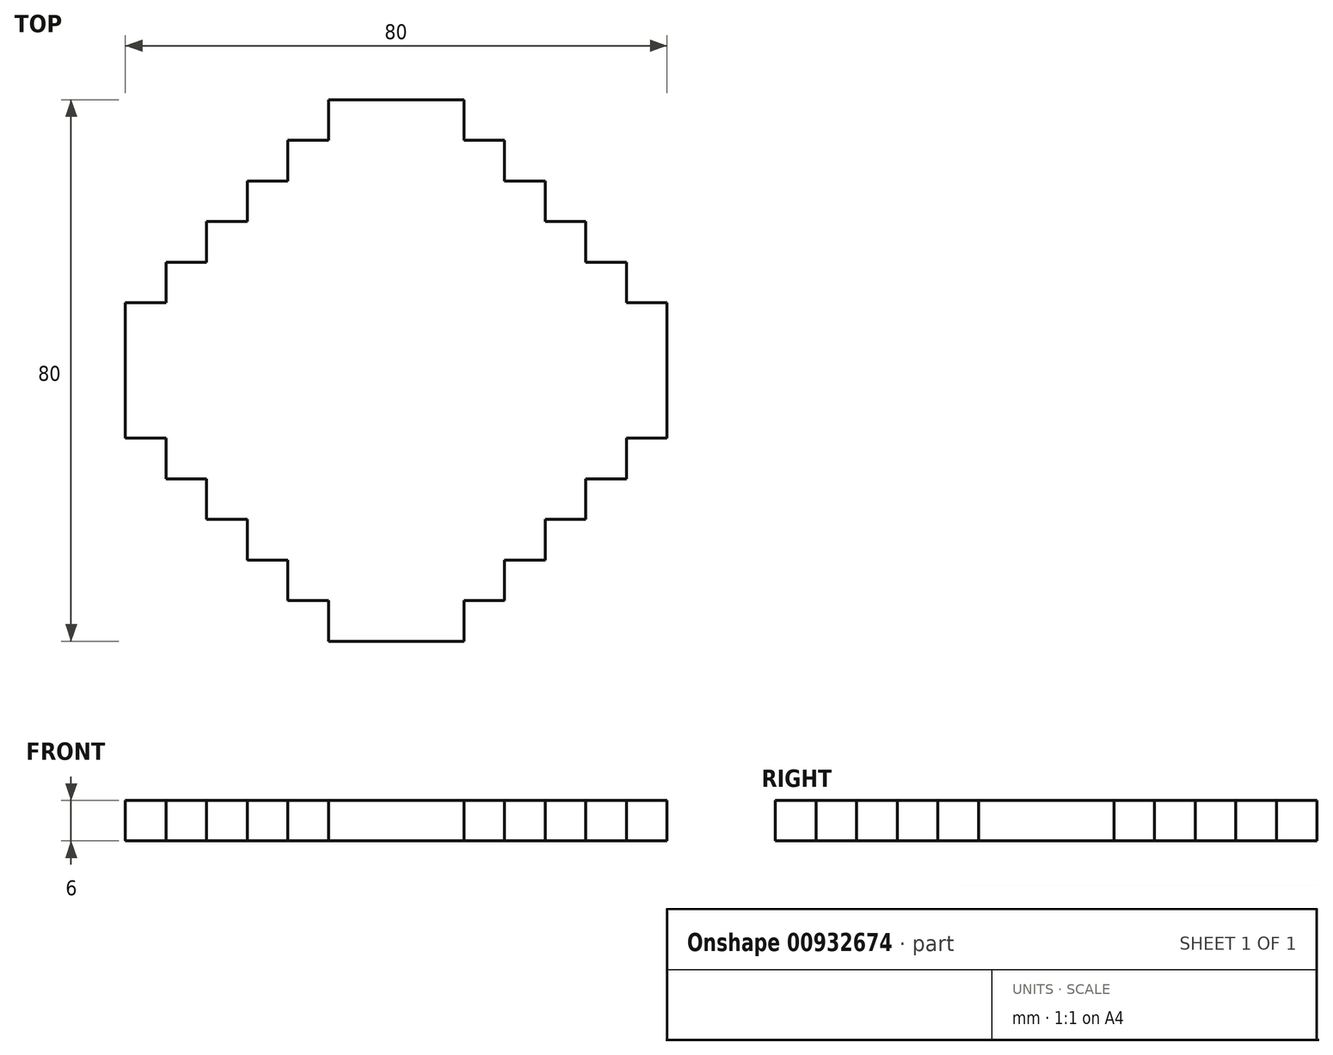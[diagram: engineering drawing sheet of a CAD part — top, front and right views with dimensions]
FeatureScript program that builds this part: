
annotation { "Feature Type Name" : "Feature", "Feature Type Description" : "" }
export const myFeature = defineFeature(function(context is Context, id is Id, definition is map)
    precondition{}
    {
        {
            var Q0;
            Q0=qCreatedBy(makeId("Top.planeOp"),FACE);
            var sketch = newSketch(context, id + "F0", { "sketchPlane" : qUnion([Q0])});
            skLineSegment(sketch, "E0.bottom", {"start": v(-10, 40) * mm, "end": v(10, 40) * mm});
            skLineSegment(sketch, "E0.top", {"start": v(-10, -40) * mm, "end": v(10, -40) * mm});
            skPoint(sketch, "E0.middle", {"position": v(0, 0) * mm});
            skLineSegment(sketch, "E1.top", {"start": v(10, 34) * mm, "end": v(16, 34) * mm});
            skLineSegment(sketch, "E1.left", {"start": v(10, 40) * mm, "end": v(10, 34) * mm});
            skLineSegment(sketch, "E2.top", {"start": v(16, 28) * mm, "end": v(22, 28) * mm});
            skLineSegment(sketch, "E2.left", {"start": v(16, 34) * mm, "end": v(16, 28) * mm});
            skLineSegment(sketch, "E3.top", {"start": v(22, 22) * mm, "end": v(28, 22) * mm});
            skLineSegment(sketch, "E3.left", {"start": v(22, 28) * mm, "end": v(22, 22) * mm});
            skLineSegment(sketch, "E4.top", {"start": v(28, 16) * mm, "end": v(34, 16) * mm});
            skLineSegment(sketch, "E4.left", {"start": v(28, 22) * mm, "end": v(28, 16) * mm});
            skLineSegment(sketch, "E5.top", {"start": v(34, 10) * mm, "end": v(40, 10) * mm});
            skLineSegment(sketch, "E5.left", {"start": v(34, 16) * mm, "end": v(34, 10) * mm});
            skLineSegment(sketch, "E6.MirrorCS", {"start": v(-16, 34) * mm, "end": v(-16, 28) * mm});
            skLineSegment(sketch, "E7.MirrorCS", {"start": v(-10, 40) * mm, "end": v(-10, 34) * mm});
            skLineSegment(sketch, "E8.MirrorCS", {"start": v(-22, 28) * mm, "end": v(-22, 22) * mm});
            skLineSegment(sketch, "E9.MirrorCS", {"start": v(-34, 16) * mm, "end": v(-34, 10) * mm});
            skLineSegment(sketch, "E10.MirrorCS", {"start": v(-28, 22) * mm, "end": v(-28, 16) * mm});
            skLineSegment(sketch, "E11.MirrorCS", {"start": v(-22, 22) * mm, "end": v(-28, 22) * mm});
            skLineSegment(sketch, "E12.MirrorCS", {"start": v(-28, 16) * mm, "end": v(-34, 16) * mm});
            skLineSegment(sketch, "E13.MirrorCS", {"start": v(-34, 10) * mm, "end": v(-40, 10) * mm});
            skLineSegment(sketch, "E14.MirrorCS", {"start": v(-16, 28) * mm, "end": v(-22, 28) * mm});
            skLineSegment(sketch, "E15.MirrorCS", {"start": v(-10, 34) * mm, "end": v(-16, 34) * mm});
            skLineSegment(sketch, "E16.MirrorCS", {"start": v(-34, -10) * mm, "end": v(-40, -10) * mm});
            skLineSegment(sketch, "E17.MirrorCS", {"start": v(-28, -16) * mm, "end": v(-34, -16) * mm});
            skLineSegment(sketch, "E18.MirrorCS", {"start": v(-22, -22) * mm, "end": v(-28, -22) * mm});
            skLineSegment(sketch, "E19.MirrorCS", {"start": v(-34, -16) * mm, "end": v(-34, -10) * mm});
            skLineSegment(sketch, "E20.MirrorCS", {"start": v(-28, -22) * mm, "end": v(-28, -16) * mm});
            skLineSegment(sketch, "E21.MirrorCS", {"start": v(-22, -28) * mm, "end": v(-22, -22) * mm});
            skLineSegment(sketch, "E22.MirrorCS", {"start": v(-16, -34) * mm, "end": v(-16, -28) * mm});
            skLineSegment(sketch, "E23.MirrorCS", {"start": v(-10, -34) * mm, "end": v(-16, -34) * mm});
            skLineSegment(sketch, "E24.MirrorCS", {"start": v(-16, -28) * mm, "end": v(-22, -28) * mm});
            skLineSegment(sketch, "E25.MirrorCS", {"start": v(-10, -40) * mm, "end": v(-10, -34) * mm});
            skLineSegment(sketch, "E26.MirrorCS", {"start": v(34, -10) * mm, "end": v(40, -10) * mm});
            skLineSegment(sketch, "E27.MirrorCS", {"start": v(28, -16) * mm, "end": v(34, -16) * mm});
            skLineSegment(sketch, "E28.MirrorCS", {"start": v(22, -22) * mm, "end": v(28, -22) * mm});
            skLineSegment(sketch, "E29.MirrorCS", {"start": v(16, -28) * mm, "end": v(22, -28) * mm});
            skLineSegment(sketch, "E30.MirrorCS", {"start": v(10, -40) * mm, "end": v(10, -34) * mm});
            skLineSegment(sketch, "E31.MirrorCS", {"start": v(16, -34) * mm, "end": v(16, -28) * mm});
            skLineSegment(sketch, "E32.MirrorCS", {"start": v(10, -34) * mm, "end": v(16, -34) * mm});
            skLineSegment(sketch, "E33.MirrorCS", {"start": v(22, -28) * mm, "end": v(22, -22) * mm});
            skLineSegment(sketch, "E34.MirrorCS", {"start": v(28, -22) * mm, "end": v(28, -16) * mm});
            skLineSegment(sketch, "E35.MirrorCS", {"start": v(34, -16) * mm, "end": v(34, -10) * mm});
            skPoint(sketch, "E1.right.start.orphan", {"position": v(68.94, 60) * mm});
            skPoint(sketch, "E36.orphan", {"position": v(68.94, 34) * mm});
            skPoint(sketch, "E37.orphan", {"position": v(68.95, 40) * mm});
            skPoint(sketch, "E38.orphan", {"position": v(68.94, 50) * mm});
            skPoint(sketch, "E3.right.end.orphan", {"position": v(68.94, 22) * mm});
            skPoint(sketch, "E3.right.start.orphan", {"position": v(68.94, 40) * mm});
            skPoint(sketch, "E4.right.start.orphan", {"position": v(68.94, 30) * mm});
            skLineSegment(sketch, "E39.trimOffspring", {"start": v(40, 10) * mm, "end": v(40, -10) * mm});
            skPoint(sketch, "E0.right.start.orphan", {"position": v(68.94, 28) * mm});
            skPoint(sketch, "E40.orphan", {"position": v(40, 16) * mm});
            skPoint(sketch, "E41.orphan", {"position": v(68.94, -22) * mm});
            skPoint(sketch, "E42.orphan", {"position": v(40, -16) * mm});
            skPoint(sketch, "E43.orphan", {"position": v(68.94, -28) * mm});
            skPoint(sketch, "E44.MirrorCS.end.orphan", {"position": v(68.94, -40) * mm});
            skPoint(sketch, "E44.MirrorCS.start.orphan", {"position": v(22, -28) * mm});
            skPoint(sketch, "E45.MirrorCS.end.orphan", {"position": v(68.94, -50) * mm});
            skPoint(sketch, "E46.trimOffspring.end.orphan", {"position": v(68.53, -40) * mm});
            skPoint(sketch, "E46.trimOffspring.start.orphan", {"position": v(68.94, -34) * mm});
            skPoint(sketch, "E47.MirrorCS.end.orphan", {"position": v(68.94, -60) * mm});
            skPoint(sketch, "E48.orphan", {"position": v(-68.94, -34) * mm});
            skPoint(sketch, "E49.MirrorCS.end.orphan", {"position": v(-68.94, -50) * mm});
            skPoint(sketch, "E49.MirrorCS.start.orphan", {"position": v(-16, -34) * mm});
            skPoint(sketch, "E50.orphan", {"position": v(-68.94, -28) * mm});
            skPoint(sketch, "E51.MirrorCS.end.orphan", {"position": v(-68.94, -40) * mm});
            skPoint(sketch, "E51.MirrorCS.start.orphan", {"position": v(-22, -28) * mm});
            skPoint(sketch, "E52.trimOffspring.end.orphan", {"position": v(-68.95, -40) * mm});
            skPoint(sketch, "E53.orphan", {"position": v(-40, -16) * mm});
            skPoint(sketch, "E54.trimOffspring.end.orphan", {"position": v(-68.94, -22) * mm});
            skLineSegment(sketch, "E55.trimOffspring", {"start": v(-40, 10) * mm, "end": v(-40, -10) * mm});
            skPoint(sketch, "E56.orphan", {"position": v(-68.53, 40) * mm});
            skPoint(sketch, "E57.orphan", {"position": v(-68.94, 34) * mm});
            skPoint(sketch, "E58.orphan", {"position": v(-68.94, 28) * mm});
            skPoint(sketch, "E59.MirrorCS.end.orphan", {"position": v(-68.94, 40) * mm});
            skPoint(sketch, "E60.orphan", {"position": v(-68.94, 22) * mm});
            skPoint(sketch, "E61.MirrorCS.end.orphan", {"position": v(-68.94, 30) * mm});
            skPoint(sketch, "E61.MirrorCS.start.orphan", {"position": v(-28, 22) * mm});
            skPoint(sketch, "E62.MirrorCS.end.orphan", {"position": v(-68.94, 50) * mm});
            skPoint(sketch, "E63.orphan", {"position": v(-40, 16) * mm});
            skPoint(sketch, "E64.MirrorCS.start.orphan", {"position": v(-28, 16) * mm});
            skSolve(sketch);
        }
        {
            var Q0;
            Q0=makeQuery(id+"F0.imprint","IMPRINT",FACE,{"disambiguationData":[TD([[makeQuery(id+"F0.imprint","IMPRINT",EDGE,{"derivedFrom":sQuery(id+"F0.wireOp",EDGE,"E0.bottom")}),-1.0]])]});
            extrude(context, id + "F1", {"entities" : qUnion([Q0]), "depth" : 6 * mm, "offsetDistance" : 25 * mm});
        }
    });
